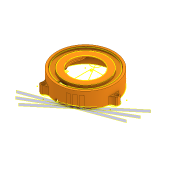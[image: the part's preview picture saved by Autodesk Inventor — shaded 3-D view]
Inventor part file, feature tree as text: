
AUTODESK INVENTOR PART (.ipt)
format: ipt  version: 2020.3 (Build 243373000, 373)  size: 294,400 bytes
history: native  units: mm
features: sketch x9, other x3, plane x3
ambient origin geometry x8: Origin, YZ Plane, XZ Plane, XY Plane, X Axis, Y Axis, Z Axis, Center Point
bodies: Solid1 (feature_tree)
feature tree (15):
  other  "Door-TopPart.ipt"
  other  "Solid2::Door-TopPart.ipt"
  other  "TaggingFeature1"
  sketch  "Sketch1"  dims[d0=10.0mm]
  sketch  "Sketch2"
  sketch  "Sketch3"
  sketch  "Sketch4"
  sketch  "Sketch5"
  sketch  "Sketch6"
  sketch  "Sketch7"
  sketch  "Sketch8"
  sketch  "Sketch9"
  plane  "Work Plane1"
  plane  "Work Plane2"
  plane  "Work Plane3"
